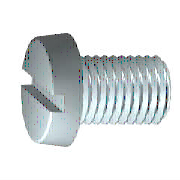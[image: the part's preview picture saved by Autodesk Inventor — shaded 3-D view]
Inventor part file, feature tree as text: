
AUTODESK INVENTOR PART (.ipt)
format: ipt  version: 2019.2 (Build 232265000, 265)  size: 178,176 bytes
history: native  units: mm (DEFAULTED — no unit token found)
features: sketch x2, other x1, extrude x1, plane x1
ambient origin geometry x7: Origin, YZ Plane, XZ Plane, X Axis, Y Axis, Z Axis, Center Point
bodies: Solid1 (feature_tree)
feature tree (5):
  other  "Körper"
  sketch  "Skizze2"  dims[d2=0.24548mm d3=1.3mm d4=2.0mm d5=1.783494mm d8=90.0deg d7=0.0mm d9=3.8mm d10=0.872665mm d11=0.5mm d12=3.8mm d14=0.1mm d15=19.2mm d16=0.0mm d17=0.216505mm d18=0.24548mm d19=0.6mm d20=0.0mm d36=45.0deg d37=0.0mm d39=0.0mm]
  extrude  "Loch"  Depth=19.2mm
  plane  "Work Plane1"
  sketch  "Skizze1"  dims[d0=20.0mm d1=19.2mm]
